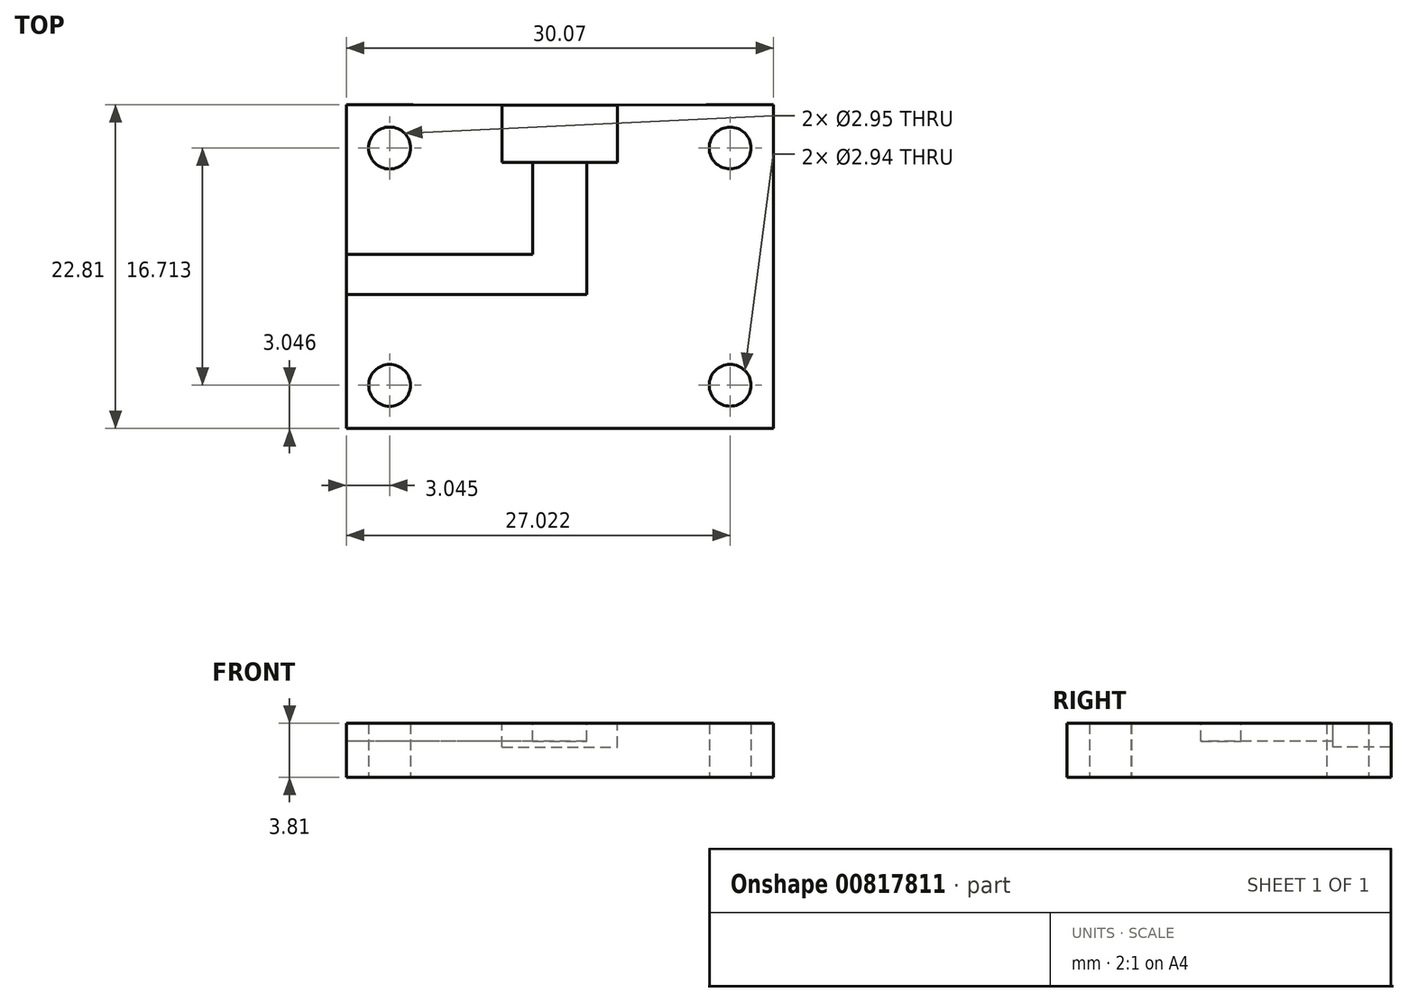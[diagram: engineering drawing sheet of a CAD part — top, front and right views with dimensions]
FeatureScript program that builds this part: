
annotation { "Feature Type Name" : "Feature", "Feature Type Description" : "" }
export const myFeature = defineFeature(function(context is Context, id is Id, definition is map)
    precondition{}
    {
        {
            var Q0;
            Q0=qCreatedBy(makeId("Top.planeOp"),FACE);
            var sketch = newSketch(context, id + "F0", { "sketchPlane" : qUnion([Q0])});
            skLineSegment(sketch, "E0.bottom", {"start": v(10.31, -9.2) * mm, "end": v(-10.31, -9.2) * mm});
            skLineSegment(sketch, "E0.left", {"start": v(10.31, -9.2) * mm, "end": v(10.31, 9.2) * mm});
            skLineSegment(sketch, "E0.right", {"start": v(-10.31, -9.2) * mm, "end": v(-10.31, 9.2) * mm});
            skPoint(sketch, "E0.middle", {"position": v(0, 0) * mm});
            skLineSegment(sketch, "E1.bottom", {"start": v(4.06, 3.08) * mm, "end": v(-4.06, 3.08) * mm});
            skLineSegment(sketch, "E1.left", {"start": v(4.06, 3.08) * mm, "end": v(4.06, 9.18) * mm});
            skLineSegment(sketch, "E1.right", {"start": v(-4.06, 3.08) * mm, "end": v(-4.06, 9.18) * mm});
            skPoint(sketch, "E1.middle", {"position": v(0, 6.13) * mm});
            skLineSegment(sketch, "E2", {"start": v(-10.31, 9.2) * mm, "end": v(-4.06, 9.18) * mm});
            skLineSegment(sketch, "E3", {"start": v(4.06, 9.18) * mm, "end": v(10.31, 9.2) * mm});
            skSolve(sketch);
        }
        {
            var Q0;
            Q0=makeQuery(id+"F0.imprint","IMPRINT",FACE,{"disambiguationData":[TD([[makeQuery(id+"F0.imprint","IMPRINT",EDGE,{"derivedFrom":sQuery(id+"F0.wireOp",EDGE,"E0.bottom")}),-1.0]])]});
            extrude(context, id + "F1", {"entities" : qUnion([Q0]), "depth" : 3.8 * mm, "offsetDistance" : 25.4 * mm});
        }
        {
            var Q0;
            Q0=makeQuery(id+"F1.opExtrude","SWEPT_FACE",FACE,{"disambiguationData":[OSD([sQuery(id+"F0.wireOp",EDGE,"E1.bottom")])]});
            var sketch = newSketch(context, id + "F2", { "sketchPlane" : qUnion([Q0])});
            skLineSegment(sketch, "E4.bottom", {"start": v(4.06, 3.81) * mm, "end": v(-4.06, 3.81) * mm});
            skLineSegment(sketch, "E4.top", {"start": v(4.06, 1.9) * mm, "end": v(-4.06, 1.9) * mm});
            skLineSegment(sketch, "E4.left", {"start": v(4.06, 3.81) * mm, "end": v(4.06, 1.9) * mm});
            skLineSegment(sketch, "E4.right", {"start": v(-4.06, 3.81) * mm, "end": v(-4.06, 1.9) * mm});
            skSolve(sketch);
        }
        {
            var Q0;
            Q0=makeQuery(id+"F2.imprint","IMPRINT",FACE,{"disambiguationData":[TD([[makeQuery(id+"F2.imprint","IMPRINT",EDGE,{"derivedFrom":sQuery(id+"F2.wireOp",EDGE,"E4.bottom")}),-1.0]])]});
            var Q1;
            Q1=makeQuery(id+"F1.opExtrude","SWEPT_FACE",FACE,{"disambiguationData":[OSD([sQuery(id+"F0.wireOp",EDGE,"E0.bottom")])]});
            extrude(context, id + "F3", {"entities" : qUnion([Q0, Q1]), "operationType" : NewBodyOperationType.ADD, "oppositeDirection" : true, "depth" : 1.85 * mm, "offsetDistance" : 25.4 * mm});
        }
        {
            var Q0;
            {var subQ0=sQuery(id+"F0.wireOp",EDGE,"E0.right");Q0=makeQuery(id+"F3.boolean.opBoolean","MERGE",FACE,{"derivedFrom":[makeQuery(id+"F1.opExtrude","SWEPT_FACE",FACE,{"disambiguationData":[OSD([subQ0])]}),makeQuery(id+"F3.opExtrude","SWEPT_FACE",FACE,{"disambiguationData":[OSD([sQuery(id+"F0.wireOp",EDGE,"E0.bottom"),subQ0])]})]});}
            extrude(context, id + "F4", {"entities" : qUnion([Q0]), "operationType" : NewBodyOperationType.ADD, "depth" : 2.18 * mm, "offsetDistance" : 25.4 * mm});
        }
        {
            var Q0;
            {var subQ0=sQuery(id+"F0.wireOp",EDGE,"E0.left");Q0=makeQuery(id+"F3.boolean.opBoolean","MERGE",FACE,{"derivedFrom":[makeQuery(id+"F1.opExtrude","SWEPT_FACE",FACE,{"disambiguationData":[OSD([subQ0])]}),makeQuery(id+"F3.opExtrude","SWEPT_FACE",FACE,{"disambiguationData":[OSD([sQuery(id+"F0.wireOp",EDGE,"E0.bottom"),subQ0])]})]});}
            extrude(context, id + "F5", {"entities" : qUnion([Q0]), "operationType" : NewBodyOperationType.ADD, "depth" : 2.18 * mm, "offsetDistance" : 25.4 * mm});
        }
        {
            var Q0;
            Q0=makeQuery(id+"F1.opExtrude","SWEPT_FACE",FACE,{"disambiguationData":[OSD([sQuery(id+"F0.wireOp",EDGE,"E1.bottom")])]});
            var sketch = newSketch(context, id + "F6", { "sketchPlane" : qUnion([Q0])});
            skLineSegment(sketch, "E5.bottom", {"start": v(-4.06, 3.81) * mm, "end": v(4.06, 3.81) * mm});
            skLineSegment(sketch, "E5.top", {"start": v(-4.06, 1.68) * mm, "end": v(4.06, 1.68) * mm});
            skLineSegment(sketch, "E5.left", {"start": v(-4.06, 3.81) * mm, "end": v(-4.06, 1.68) * mm});
            skLineSegment(sketch, "E5.right", {"start": v(4.06, 3.81) * mm, "end": v(4.06, 1.68) * mm});
            skSolve(sketch);
        }
        {
            var Q0;
            Q0=makeQuery(id+"F6.imprint","IMPRINT",FACE,{"disambiguationData":[TD([[makeQuery(id+"F6.imprint","IMPRINT",EDGE,{"derivedFrom":sQuery(id+"F6.wireOp",EDGE,"E5.bottom")}),-1.0]])]});
            extrude(context, id + "F7", {"entities" : qUnion([Q0]), "operationType" : NewBodyOperationType.ADD, "depth" : 6.1 * mm, "offsetDistance" : 25.4 * mm});
        }
        {
            var Q0;
            Q0=makeQuery(id+"F4.opExtrude","CAP_FACE",FACE,{"disambiguationData":[OSD([sQuery(id+"F0.wireOp",EDGE,"E0.bottom"),sQuery(id+"F0.wireOp",EDGE,"E0.right")])],"isStart":false});
            extrude(context, id + "F8", {"entities" : qUnion([Q0]), "operationType" : NewBodyOperationType.ADD, "depth" : 2.54 * mm, "offsetDistance" : 25.4 * mm});
        }
        {
            var Q0;
            Q0=makeQuery(id+"F5.opExtrude","CAP_FACE",FACE,{"disambiguationData":[OSD([sQuery(id+"F0.wireOp",EDGE,"E0.bottom"),sQuery(id+"F0.wireOp",EDGE,"E0.left")])],"isStart":false});
            extrude(context, id + "F9", {"entities" : qUnion([Q0]), "operationType" : NewBodyOperationType.ADD, "depth" : 2.54 * mm, "offsetDistance" : 25.4 * mm});
        }
        {
            var Q0;
            {var subQ0=sQuery(id+"F0.wireOp",EDGE,"E0.left");var subQ1=sQuery(id+"F0.wireOp",EDGE,"E0.bottom");var subQ2=makeQuery(id+"F3.opExtrude","CAP_EDGE",EDGE,{"disambiguationData":[OSD([subQ1,subQ0])],"isStart":false});var subQ3=sQuery(id+"F0.wireOp",EDGE,"E0.right");var subQ4=makeQuery(id+"F3.opExtrude","CAP_EDGE",EDGE,{"disambiguationData":[OSD([subQ1,subQ3])],"isStart":false});Q0=makeQuery(id+"F9.boolean.opBoolean","MERGE",FACE,{"derivedFrom":[makeQuery(id+"F8.boolean.opBoolean","MERGE",FACE,{"derivedFrom":[makeQuery(id+"F5.boolean.opBoolean","MERGE",FACE,{"derivedFrom":[makeQuery(id+"F4.boolean.opBoolean","MERGE",FACE,{"derivedFrom":[makeQuery(id+"F3.opExtrude","CAP_FACE",FACE,{"disambiguationData":[OSD([subQ1])],"isStart":false}),makeQuery(id+"F4.opExtrude","SWEPT_FACE",FACE,{"disambiguationData":[OSD([subQ1,subQ3]),TDD([subQ4])]})]}),makeQuery(id+"F5.opExtrude","SWEPT_FACE",FACE,{"disambiguationData":[OSD([subQ1,subQ0]),TDD([subQ2])]})]}),makeQuery(id+"F8.opExtrude","SWEPT_FACE",FACE,{"disambiguationData":[OSD([subQ1,subQ3]),TDD([makeQuery(id+"F4.opExtrude","CAP_EDGE",EDGE,{"disambiguationData":[OSD([subQ1,subQ3]),TDD([subQ4])],"isStart":false})])]})]}),makeQuery(id+"F9.opExtrude","SWEPT_FACE",FACE,{"disambiguationData":[OSD([subQ1,subQ0]),TDD([makeQuery(id+"F5.opExtrude","CAP_EDGE",EDGE,{"disambiguationData":[OSD([subQ1,subQ0]),TDD([subQ2])],"isStart":false})])]})]});}
            extrude(context, id + "F10", {"entities" : qUnion([Q0]), "operationType" : NewBodyOperationType.ADD, "depth" : 2.54 * mm, "offsetDistance" : 25.4 * mm});
        }
        {
            var Q0;
            Q0=makeQuery(id+"F1.opExtrude","SWEPT_FACE",FACE,{"disambiguationData":[OSD([sQuery(id+"F0.wireOp",EDGE,"E1.bottom")])]});
            extrude(context, id + "F11", {"entities" : qUnion([Q0]), "operationType" : NewBodyOperationType.REMOVE, "depth" : 6.1 * mm, "offsetDistance" : 25.4 * mm});
        }
        {
            var Q0;
            {var subQ0=sQuery(id+"F0.wireOp",EDGE,"E0.left");var subQ1=sQuery(id+"F0.wireOp",EDGE,"E0.bottom");var subQ2=makeQuery(id+"F1.opExtrude","CAP_VERTEX",VERTEX,{"disambiguationData":[OSD([subQ1,subQ0])],"isStart":false});var subQ3=makeQuery(id+"F3.opExtrude","CAP_VERTEX",VERTEX,{"disambiguationData":[OSD([subQ1,subQ0]),TDD([subQ2])],"isStart":false});var subQ4=sQuery(id+"F0.wireOp",EDGE,"E0.right");var subQ5=makeQuery(id+"F1.opExtrude","CAP_VERTEX",VERTEX,{"disambiguationData":[OSD([subQ1,subQ4])],"isStart":false});var subQ6=makeQuery(id+"F3.opExtrude","CAP_VERTEX",VERTEX,{"disambiguationData":[OSD([subQ1,subQ4]),TDD([subQ5])],"isStart":false});var subQ7=makeQuery(id+"F1.opExtrude","CAP_EDGE",EDGE,{"disambiguationData":[OSD([subQ1])],"isStart":false});var subQ8=makeQuery(id+"F3.boolean.opBoolean","MERGE",EDGE,{"derivedFrom":[makeQuery(id+"F1.opExtrude","CAP_EDGE",EDGE,{"disambiguationData":[OSD([subQ0])],"isStart":false}),makeQuery(id+"F3.opExtrude","SWEPT_EDGE",EDGE,{"disambiguationData":[OSD([subQ1,subQ0]),TDD([subQ2])]})]});var subQ9=makeQuery(id+"F3.boolean.opBoolean","MERGE",EDGE,{"derivedFrom":[makeQuery(id+"F1.opExtrude","CAP_EDGE",EDGE,{"disambiguationData":[OSD([subQ4])],"isStart":false}),makeQuery(id+"F3.opExtrude","SWEPT_EDGE",EDGE,{"disambiguationData":[OSD([subQ1,subQ4]),TDD([subQ5])]})]});Q0=makeQuery(id+"F10.boolean.opBoolean","MERGE",FACE,{"derivedFrom":[makeQuery(id+"F9.boolean.opBoolean","MERGE",FACE,{"derivedFrom":[makeQuery(id+"F8.boolean.opBoolean","MERGE",FACE,{"derivedFrom":[makeQuery(id+"F7.boolean.opBoolean","MERGE",FACE,{"derivedFrom":[makeQuery(id+"F5.boolean.opBoolean","MERGE",FACE,{"derivedFrom":[makeQuery(id+"F4.boolean.opBoolean","MERGE",FACE,{"derivedFrom":[makeQuery(id+"F3.boolean.opBoolean","MERGE",FACE,{"derivedFrom":[makeQuery(id+"F1.opExtrude","CAP_FACE",FACE,{"disambiguationData":[OSD([subQ1,subQ0,subQ4,sQuery(id+"F0.wireOp",EDGE,"E1.bottom"),sQuery(id+"F0.wireOp",EDGE,"E1.left"),sQuery(id+"F0.wireOp",EDGE,"E1.right"),sQuery(id+"F0.wireOp",EDGE,"E2"),sQuery(id+"F0.wireOp",EDGE,"E3")])],"isStart":false}),makeQuery(id+"F3.opExtrude","SWEPT_FACE",FACE,{"disambiguationData":[OSD([subQ1]),TDD([subQ7])]})]}),makeQuery(id+"F4.opExtrude","SWEPT_FACE",FACE,{"disambiguationData":[OSD([subQ1,subQ4]),TDD([subQ9])]})]}),makeQuery(id+"F5.opExtrude","SWEPT_FACE",FACE,{"disambiguationData":[OSD([subQ1,subQ0]),TDD([subQ8])]})]}),makeQuery(id+"F7.opExtrude","SWEPT_FACE",FACE,{"disambiguationData":[OSD([sQuery(id+"F6.wireOp",EDGE,"E5.bottom")])]})]}),makeQuery(id+"F8.opExtrude","SWEPT_FACE",FACE,{"disambiguationData":[OSD([subQ1,subQ4]),TDD([makeQuery(id+"F4.opExtrude","CAP_EDGE",EDGE,{"disambiguationData":[OSD([subQ1,subQ4]),TDD([subQ9])],"isStart":false})])]})]}),makeQuery(id+"F9.opExtrude","SWEPT_FACE",FACE,{"disambiguationData":[OSD([subQ1,subQ0]),TDD([makeQuery(id+"F5.opExtrude","CAP_EDGE",EDGE,{"disambiguationData":[OSD([subQ1,subQ0]),TDD([subQ8])],"isStart":false})])]})]}),makeQuery(id+"F10.opExtrude","SWEPT_FACE",FACE,{"disambiguationData":[OSD([subQ1,subQ0,subQ4]),TDD([makeQuery(id+"F9.boolean.opBoolean","MERGE",EDGE,{"derivedFrom":[makeQuery(id+"F8.boolean.opBoolean","MERGE",EDGE,{"derivedFrom":[makeQuery(id+"F5.boolean.opBoolean","MERGE",EDGE,{"derivedFrom":[makeQuery(id+"F4.boolean.opBoolean","MERGE",EDGE,{"derivedFrom":[makeQuery(id+"F3.opExtrude","CAP_EDGE",EDGE,{"disambiguationData":[OSD([subQ1]),TDD([subQ7])],"isStart":false}),makeQuery(id+"F4.opExtrude","SWEPT_EDGE",EDGE,{"disambiguationData":[OSD([subQ1,subQ4]),TDD([subQ6])]})]}),makeQuery(id+"F5.opExtrude","SWEPT_EDGE",EDGE,{"disambiguationData":[OSD([subQ1,subQ0]),TDD([subQ3])]})]}),makeQuery(id+"F8.opExtrude","SWEPT_EDGE",EDGE,{"disambiguationData":[OSD([subQ1,subQ4]),TDD([makeQuery(id+"F4.opExtrude","CAP_VERTEX",VERTEX,{"disambiguationData":[OSD([subQ1,subQ4]),TDD([subQ6])],"isStart":false})])]})]}),makeQuery(id+"F9.opExtrude","SWEPT_EDGE",EDGE,{"disambiguationData":[OSD([subQ1,subQ0]),TDD([makeQuery(id+"F5.opExtrude","CAP_VERTEX",VERTEX,{"disambiguationData":[OSD([subQ1,subQ0]),TDD([subQ3])],"isStart":false})])]})]})])]})]});}
            var sketch = newSketch(context, id + "F12", { "sketchPlane" : qUnion([Q0])});
            skCircle(sketch, "E6", {"center": v(11.99, -10.55) * mm, "radius": 1.47 * mm});
            skCircle(sketch, "E7", {"center": v(-11.99, -10.55) * mm, "radius": 1.47 * mm});
            skCircle(sketch, "E8", {"center": v(11.99, 6.16) * mm, "radius": 1.48 * mm});
            skCircle(sketch, "E9", {"center": v(-11.99, 6.16) * mm, "radius": 1.47 * mm});
            skSolve(sketch);
        }
        {
            var Q0;
            Q0=makeQuery(id+"F12.imprint","IMPRINT",FACE,{"disambiguationData":[TD([[makeQuery(id+"F12.imprint","IMPRINT",EDGE,{"derivedFrom":sQuery(id+"F12.wireOp",EDGE,"E6")}),1.0]])]});
            var Q1;
            Q1=makeQuery(id+"F12.imprint","IMPRINT",FACE,{"disambiguationData":[TD([[makeQuery(id+"F12.imprint","IMPRINT",EDGE,{"derivedFrom":sQuery(id+"F12.wireOp",EDGE,"E7")}),1.0]])]});
            var Q2;
            Q2=makeQuery(id+"F12.imprint","IMPRINT",FACE,{"disambiguationData":[TD([[makeQuery(id+"F12.imprint","IMPRINT",EDGE,{"derivedFrom":sQuery(id+"F12.wireOp",EDGE,"E8")}),1.0]])]});
            var Q3;
            Q3=makeQuery(id+"F12.imprint","IMPRINT",FACE,{"disambiguationData":[TD([[makeQuery(id+"F12.imprint","IMPRINT",EDGE,{"derivedFrom":sQuery(id+"F12.wireOp",EDGE,"E9")}),1.0]])]});
            extrude(context, id + "F13", {"entities" : qUnion([Q0, Q1, Q2, Q3]), "operationType" : NewBodyOperationType.REMOVE, "oppositeDirection" : true, "depth" : 25.4 * mm, "offsetDistance" : 25.4 * mm});
        }
        {
            var Q0;
            Q0=makeQuery(id+"F1.opExtrude","SWEPT_BODY",BODY,{"disambiguationData":[OSD([sQuery(id+"F0.wireOp",EDGE,"E0.bottom"),sQuery(id+"F0.wireOp",EDGE,"E0.left"),sQuery(id+"F0.wireOp",EDGE,"E0.right"),sQuery(id+"F0.wireOp",EDGE,"E1.bottom"),sQuery(id+"F0.wireOp",EDGE,"E1.left"),sQuery(id+"F0.wireOp",EDGE,"E1.right"),sQuery(id+"F0.wireOp",EDGE,"E2"),sQuery(id+"F0.wireOp",EDGE,"E3")])]});
            transform(context, id + "F14", {"entities" : qUnion([Q0]), "transformType" : TransformType.TRANSLATION_3D, "dx" : 0 * mm, "dy" : -28.96 * mm, "dz" : 0 * mm, "makeCopy" : true});
        }
        {
            var Q0;
            Q0=makeQuery(id+"F14.opPattern","COPY",BODY,{"derivedFrom":makeQuery(id+"F1.opExtrude","SWEPT_BODY",BODY,{"disambiguationData":[OSD([sQuery(id+"F0.wireOp",EDGE,"E0.bottom"),sQuery(id+"F0.wireOp",EDGE,"E0.left"),sQuery(id+"F0.wireOp",EDGE,"E0.right"),sQuery(id+"F0.wireOp",EDGE,"E1.bottom"),sQuery(id+"F0.wireOp",EDGE,"E1.left"),sQuery(id+"F0.wireOp",EDGE,"E1.right"),sQuery(id+"F0.wireOp",EDGE,"E2"),sQuery(id+"F0.wireOp",EDGE,"E3")])]}),"instanceName":"1"});
            deleteBodies(context, id + "F15", {"entities" : qUnion([Q0])});
        }
        {
            var Q0;
            Q0=makeQuery(id+"F1.opExtrude","SWEPT_FACE",FACE,{"disambiguationData":[OSD([sQuery(id+"F0.wireOp",EDGE,"E1.bottom")])]});
            extrude(context, id + "F16", {"entities" : qUnion([Q0]), "operationType" : NewBodyOperationType.ADD, "depth" : 2.06 * mm, "offsetDistance" : 25.4 * mm});
        }
        {
            var Q0;
            {var subQ0=sQuery(id+"F0.wireOp",EDGE,"E1.bottom");var subQ1=sQuery(id+"F0.wireOp",EDGE,"E0.left");var subQ2=sQuery(id+"F0.wireOp",EDGE,"E0.bottom");var subQ3=makeQuery(id+"F1.opExtrude","CAP_VERTEX",VERTEX,{"disambiguationData":[OSD([subQ2,subQ1])],"isStart":true});var subQ4=makeQuery(id+"F3.opExtrude","CAP_VERTEX",VERTEX,{"disambiguationData":[OSD([subQ2,subQ1]),TDD([subQ3])],"isStart":false});var subQ5=sQuery(id+"F0.wireOp",EDGE,"E0.right");var subQ6=makeQuery(id+"F1.opExtrude","CAP_VERTEX",VERTEX,{"disambiguationData":[OSD([subQ2,subQ5])],"isStart":true});var subQ7=makeQuery(id+"F3.opExtrude","CAP_VERTEX",VERTEX,{"disambiguationData":[OSD([subQ2,subQ5]),TDD([subQ6])],"isStart":false});var subQ8=makeQuery(id+"F1.opExtrude","CAP_EDGE",EDGE,{"disambiguationData":[OSD([subQ2])],"isStart":true});var subQ9=makeQuery(id+"F3.boolean.opBoolean","MERGE",EDGE,{"derivedFrom":[makeQuery(id+"F1.opExtrude","CAP_EDGE",EDGE,{"disambiguationData":[OSD([subQ1])],"isStart":true}),makeQuery(id+"F3.opExtrude","SWEPT_EDGE",EDGE,{"disambiguationData":[OSD([subQ2,subQ1]),TDD([subQ3])]})]});var subQ10=makeQuery(id+"F3.boolean.opBoolean","MERGE",EDGE,{"derivedFrom":[makeQuery(id+"F1.opExtrude","CAP_EDGE",EDGE,{"disambiguationData":[OSD([subQ5])],"isStart":true}),makeQuery(id+"F3.opExtrude","SWEPT_EDGE",EDGE,{"disambiguationData":[OSD([subQ2,subQ5]),TDD([subQ6])]})]});Q0=makeQuery(id+"F16.boolean.opBoolean","MERGE",FACE,{"derivedFrom":[makeQuery(id+"F10.boolean.opBoolean","MERGE",FACE,{"derivedFrom":[makeQuery(id+"F9.boolean.opBoolean","MERGE",FACE,{"derivedFrom":[makeQuery(id+"F8.boolean.opBoolean","MERGE",FACE,{"derivedFrom":[makeQuery(id+"F5.boolean.opBoolean","MERGE",FACE,{"derivedFrom":[makeQuery(id+"F4.boolean.opBoolean","MERGE",FACE,{"derivedFrom":[makeQuery(id+"F3.boolean.opBoolean","MERGE",FACE,{"derivedFrom":[makeQuery(id+"F1.opExtrude","CAP_FACE",FACE,{"disambiguationData":[OSD([subQ2,subQ1,subQ5,subQ0,sQuery(id+"F0.wireOp",EDGE,"E1.left"),sQuery(id+"F0.wireOp",EDGE,"E1.right"),sQuery(id+"F0.wireOp",EDGE,"E2"),sQuery(id+"F0.wireOp",EDGE,"E3")])],"isStart":true}),makeQuery(id+"F3.opExtrude","SWEPT_FACE",FACE,{"disambiguationData":[OSD([subQ2]),TDD([subQ8])]})]}),makeQuery(id+"F4.opExtrude","SWEPT_FACE",FACE,{"disambiguationData":[OSD([subQ2,subQ5]),TDD([subQ10])]})]}),makeQuery(id+"F5.opExtrude","SWEPT_FACE",FACE,{"disambiguationData":[OSD([subQ2,subQ1]),TDD([subQ9])]})]}),makeQuery(id+"F8.opExtrude","SWEPT_FACE",FACE,{"disambiguationData":[OSD([subQ2,subQ5]),TDD([makeQuery(id+"F4.opExtrude","CAP_EDGE",EDGE,{"disambiguationData":[OSD([subQ2,subQ5]),TDD([subQ10])],"isStart":false})])]})]}),makeQuery(id+"F9.opExtrude","SWEPT_FACE",FACE,{"disambiguationData":[OSD([subQ2,subQ1]),TDD([makeQuery(id+"F5.opExtrude","CAP_EDGE",EDGE,{"disambiguationData":[OSD([subQ2,subQ1]),TDD([subQ9])],"isStart":false})])]})]}),makeQuery(id+"F10.opExtrude","SWEPT_FACE",FACE,{"disambiguationData":[OSD([subQ2,subQ1,subQ5]),TDD([makeQuery(id+"F9.boolean.opBoolean","MERGE",EDGE,{"derivedFrom":[makeQuery(id+"F8.boolean.opBoolean","MERGE",EDGE,{"derivedFrom":[makeQuery(id+"F5.boolean.opBoolean","MERGE",EDGE,{"derivedFrom":[makeQuery(id+"F4.boolean.opBoolean","MERGE",EDGE,{"derivedFrom":[makeQuery(id+"F3.opExtrude","CAP_EDGE",EDGE,{"disambiguationData":[OSD([subQ2]),TDD([subQ8])],"isStart":false}),makeQuery(id+"F4.opExtrude","SWEPT_EDGE",EDGE,{"disambiguationData":[OSD([subQ2,subQ5]),TDD([subQ7])]})]}),makeQuery(id+"F5.opExtrude","SWEPT_EDGE",EDGE,{"disambiguationData":[OSD([subQ2,subQ1]),TDD([subQ4])]})]}),makeQuery(id+"F8.opExtrude","SWEPT_EDGE",EDGE,{"disambiguationData":[OSD([subQ2,subQ5]),TDD([makeQuery(id+"F4.opExtrude","CAP_VERTEX",VERTEX,{"disambiguationData":[OSD([subQ2,subQ5]),TDD([subQ7])],"isStart":false})])]})]}),makeQuery(id+"F9.opExtrude","SWEPT_EDGE",EDGE,{"disambiguationData":[OSD([subQ2,subQ1]),TDD([makeQuery(id+"F5.opExtrude","CAP_VERTEX",VERTEX,{"disambiguationData":[OSD([subQ2,subQ1]),TDD([subQ4])],"isStart":false})])]})]})])]})]}),makeQuery(id+"F16.opExtrude","SWEPT_FACE",FACE,{"disambiguationData":[OSD([subQ0])]})]});}
            var sketch = newSketch(context, id + "F17", { "sketchPlane" : qUnion([Q0])});
            skLineSegment(sketch, "E10", {"start": v(1.9, -5.14) * mm, "end": v(-1.9, -5.14) * mm});
            skLineSegment(sketch, "E11", {"start": v(-1.9, -5.14) * mm, "end": v(-1.9, 4.17) * mm});
            skLineSegment(sketch, "E12", {"start": v(-1.9, 4.17) * mm, "end": v(15.04, 4.17) * mm});
            skLineSegment(sketch, "E13", {"start": v(1.9, -5.14) * mm, "end": v(1.9, 1.34) * mm});
            skLineSegment(sketch, "E14", {"start": v(1.9, 1.34) * mm, "end": v(15.04, 1.34) * mm});
            skSolve(sketch);
        }
        {
            var Q0;
            Q0=makeQuery(id+"F17.imprint","IMPRINT",FACE,{"disambiguationData":[TD([[makeQuery(id+"F17.imprint","IMPRINT",EDGE,{"derivedFrom":sQuery(id+"F17.wireOp",EDGE,"E10")}),-1.0]])]});
            extrude(context, id + "F18", {"entities" : qUnion([Q0]), "operationType" : NewBodyOperationType.REMOVE, "oppositeDirection" : true, "depth" : 1.27 * mm, "offsetDistance" : 25.4 * mm});
        }
        {
            var Q0;
            Q0=makeQuery(id+"F1.opExtrude","SWEPT_BODY",BODY,{"disambiguationData":[OSD([sQuery(id+"F0.wireOp",EDGE,"E0.bottom"),sQuery(id+"F0.wireOp",EDGE,"E0.left"),sQuery(id+"F0.wireOp",EDGE,"E0.right"),sQuery(id+"F0.wireOp",EDGE,"E1.bottom"),sQuery(id+"F0.wireOp",EDGE,"E1.left"),sQuery(id+"F0.wireOp",EDGE,"E1.right"),sQuery(id+"F0.wireOp",EDGE,"E2"),sQuery(id+"F0.wireOp",EDGE,"E3")])]});
            var Q1;
            {var subQ0=sQuery(id+"F0.wireOp",EDGE,"E0.left");var subQ1=sQuery(id+"F0.wireOp",EDGE,"E0.bottom");var subQ2=makeQuery(id+"F1.opExtrude","CAP_VERTEX",VERTEX,{"disambiguationData":[OSD([subQ1,subQ0])],"isStart":true});var subQ3=makeQuery(id+"F3.opExtrude","CAP_VERTEX",VERTEX,{"disambiguationData":[OSD([subQ1,subQ0]),TDD([subQ2])],"isStart":false});var subQ4=makeQuery(id+"F5.opExtrude","CAP_VERTEX",VERTEX,{"disambiguationData":[OSD([subQ1,subQ0]),TDD([subQ3])],"isStart":false});var subQ9=makeQuery(id+"F3.boolean.opBoolean","MERGE",EDGE,{"derivedFrom":[makeQuery(id+"F1.opExtrude","CAP_EDGE",EDGE,{"disambiguationData":[OSD([subQ0])],"isStart":true}),makeQuery(id+"F3.opExtrude","SWEPT_EDGE",EDGE,{"disambiguationData":[OSD([subQ1,subQ0]),TDD([subQ2])]})]});var subQ10=makeQuery(id+"F5.opExtrude","CAP_EDGE",EDGE,{"disambiguationData":[OSD([subQ1,subQ0]),TDD([subQ9])],"isStart":false});Q1=makeQuery(id+"F18.boolean.opBoolean","SPLIT",EDGE,{"disambiguationData":[TD([makeQuery(id+"F18.opExtrude","SWEPT_FACE",FACE,{"disambiguationData":[OSD([sQuery(id+"F17.wireOp",EDGE,"E12")])]})])],"derivedFrom":makeQuery(id+"F10.boolean.opBoolean","MERGE",EDGE,{"derivedFrom":[makeQuery(id+"F9.opExtrude","CAP_EDGE",EDGE,{"disambiguationData":[OSD([subQ1,subQ0]),TDD([subQ10])],"isStart":false}),makeQuery(id+"F10.opExtrude","SWEPT_EDGE",EDGE,{"disambiguationData":[OSD([subQ1,subQ0]),TDD([makeQuery(id+"F9.opExtrude","CAP_VERTEX",VERTEX,{"disambiguationData":[OSD([subQ1,subQ0]),TDD([subQ4])],"isStart":false})])]})]})});}
            transform(context, id + "F19", {"entities" : qUnion([Q0]), "transformType" : TransformType.ROTATION, "transformAxis" : qUnion([Q1]), "angle" : 180 * degree, "oppositeDirection" : true, "makeCopy" : false});
        }
    });
